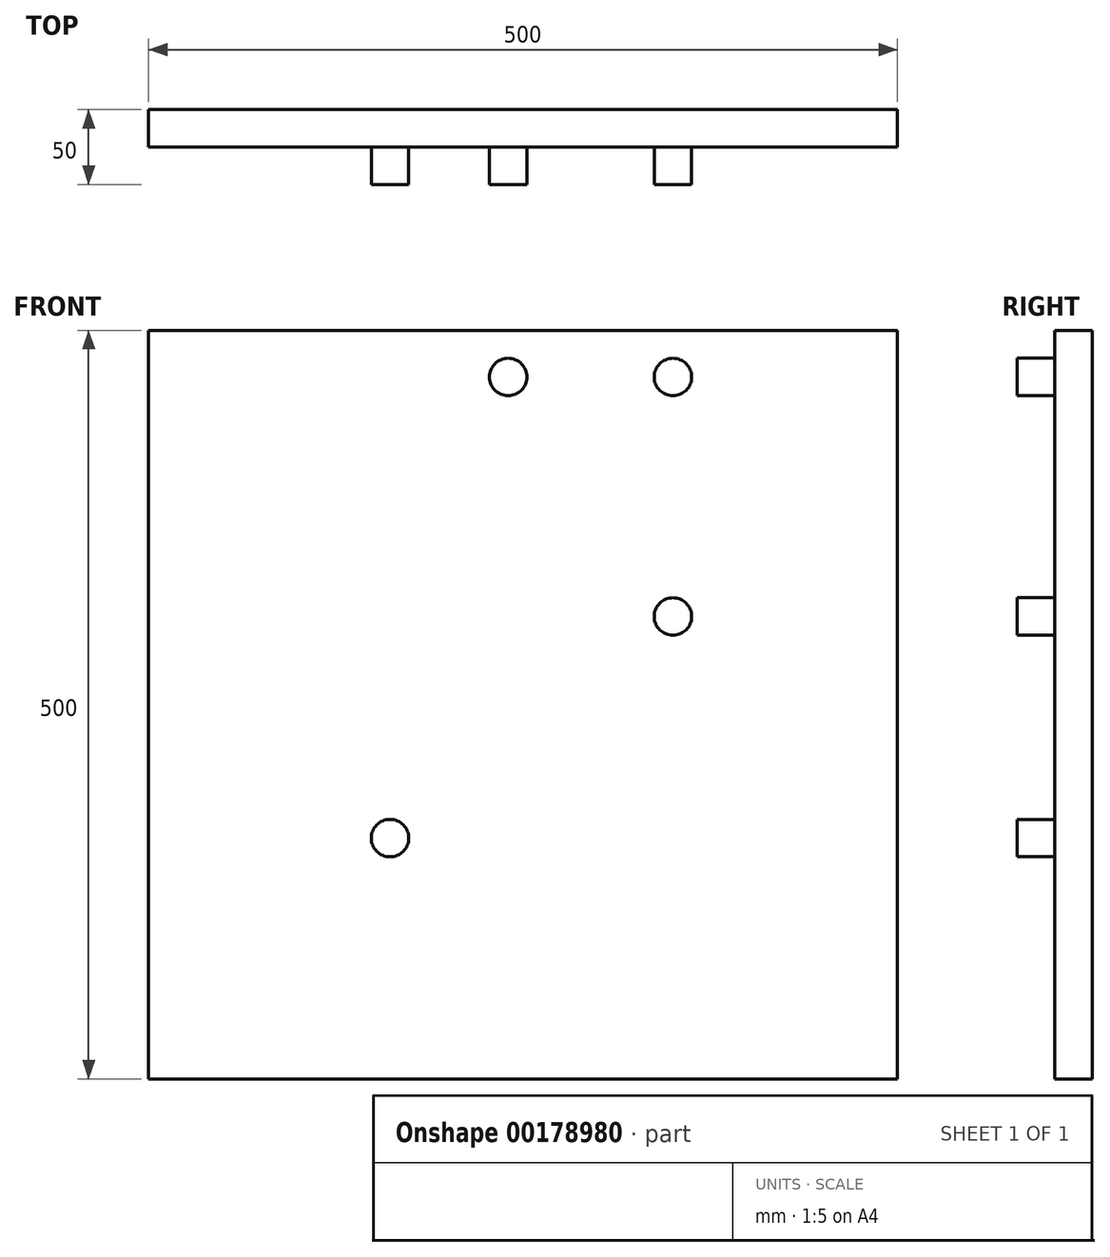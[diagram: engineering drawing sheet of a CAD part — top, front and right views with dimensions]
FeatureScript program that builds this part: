
annotation { "Feature Type Name" : "Feature", "Feature Type Description" : "" }
export const myFeature = defineFeature(function(context is Context, id is Id, definition is map)
    precondition{}
    {
        {
            var Q0;
            Q0=qCreatedBy(makeId("Front.planeOp"),FACE);
            var sketch = newSketch(context, id + "F0", { "sketchPlane" : qUnion([Q0])});
            skLineSegment(sketch, "E0.bottom", {"start": v(250, 250) * mm, "end": v(-250, 250) * mm});
            skLineSegment(sketch, "E0.top", {"start": v(250, -250) * mm, "end": v(-250, -250) * mm});
            skLineSegment(sketch, "E0.left", {"start": v(250, 250) * mm, "end": v(250, -250) * mm});
            skLineSegment(sketch, "E0.right", {"start": v(-250, 250) * mm, "end": v(-250, -250) * mm});
            skPoint(sketch, "E0.middle", {"position": v(0, 0) * mm});
            skSolve(sketch);
        }
        {
            var Q0;
            Q0=makeQuery(id+"F0.imprint","IMPRINT",FACE,{"disambiguationData":[TD([[makeQuery(id+"F0.imprint","IMPRINT",EDGE,{"derivedFrom":sQuery(id+"F0.wireOp",EDGE,"E0.bottom")}),1.0]])]});
            extrude(context, id + "F1", {"entities" : qUnion([Q0]), "depth" : 25 * mm});
        }
        {
            var Q0;
            Q0=makeQuery(id+"F1.opExtrude","CAP_FACE",FACE,{"disambiguationData":[OSD([sQuery(id+"F0.wireOp",EDGE,"E0.bottom"),sQuery(id+"F0.wireOp",EDGE,"E0.top"),sQuery(id+"F0.wireOp",EDGE,"E0.left"),sQuery(id+"F0.wireOp",EDGE,"E0.right")])],"isStart":false});
            var sketch = newSketch(context, id + "F2", { "sketchPlane" : qUnion([Q0])});
            skCircle(sketch, "E1", {"center": v(-9.9, 218.87) * mm, "radius": 12.5 * mm});
            skCircle(sketch, "E2", {"center": v(100.1, 218.87) * mm, "radius": 12.5 * mm});
            skCircle(sketch, "E3", {"center": v(100.1, 58.87) * mm, "radius": 12.5 * mm});
            skCircle(sketch, "E4", {"center": v(-88.8, -89.16) * mm, "radius": 12.5 * mm});
            skSolve(sketch);
        }
        {
            var Q0;
            Q0 = qSketchRegion(id + "F2", true);
            extrude(context, id + "F3", {"entities" : qUnion([Q0]), "operationType" : NewBodyOperationType.ADD, "depth" : 25 * mm});
        }
    });
